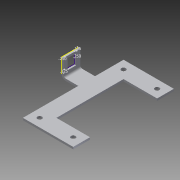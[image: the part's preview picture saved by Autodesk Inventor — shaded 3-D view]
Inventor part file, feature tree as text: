
AUTODESK INVENTOR PART (.ipt)
format: ipt  version: 2013 (Build 170138000, 138)  size: 269,312 bytes
history: native  units: in
note: dims shown in document units (in); Inventor stores cm internally (conversion verified against a paired STEP export)
features: other x9, sheet_metal_op x8, sketch x7
ambient origin geometry x8: Origin, YZ Plane, XZ Plane, XY Plane, X Axis, Y Axis, Z Axis, Center Point
bodies: Solid1 (feature_tree)
feature tree (24):
  sheet_metal_op  "Face1"
  sheet_metal_op  "Flange1"
  sheet_metal_op  "Face2"
  sketch  "Sketch4"  dims[d4=0.125in]
  sheet_metal_op  "Face3"
  sketch  "Sketch1"  dims[d0=1.0in]
  other  "Plate1"
  sketch  "Sketch2"  dims[d2=1.0in]
  other  "Plate2"
  sheet_metal_op  "Bend1"
  sheet_metal_op  "Corner1"
  sketch  "Sketch3"  dims[d3=0.125in]
  other  "Plate3"
  sheet_metal_op  "Bend2"
  sketch  "Sketch5"  dims[d5=0.0625in]
  sketch  "Sketch6"  dims[d6=0.25in]
  other  "Plate4"
  sheet_metal_op  "Bend3"
  sketch  "Sketch7"  dims[d7=0.125in d8=1.0in d9=90.0deg d10=0.125in d11=0.5in d12=0.125in d13=0.125in d14=3.3in d15=1.0in d16=6.0in d17=0.125in d18=0.125in d19=0.0625in d20=0.25in d21=0.125in d27=0.266in d28=0.5in d29=0.5in d30=0.266in d31=0.5in d32=0.5in d33=0.125in d34=0.0in d35=2.0in d36=1.0in d37=1.0in d38=2.0in d39=1.0in d40=2.0in d41=2.0in d42=1.0in d43=2.0in d44=2.0in d45=1.0in d46=0.266in d47=0.266in d48=0.266in d49=0.266in d50=0.5in d51=0.5in d52=0.5in d53=0.5in d54=0.5in d55=0.5in d56=0.5in d57=0.5in d58=0.125in d59=0.125in d60=0.0625in d61=0.25in d62=0.125in d63=0.25in d64=0.25in d65=0.125in d66=0.125in d67=0.125in d68=0.0in d69=0.125in d70=0.0in d1=0.0625in]
  other  "Cut2"
  other  "Cut3"
  other  "Cut4"
  other  "Definition1"
  other  "Cut1"
